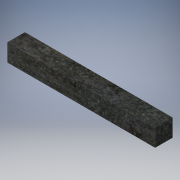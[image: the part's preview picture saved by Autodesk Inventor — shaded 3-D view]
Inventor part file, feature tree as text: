
AUTODESK INVENTOR PART (.ipt)
format: ipt  version: 2019 (Build 230136000, 136)  size: 106,496 bytes
history: native  units: mm
features: extrude x1, sketch x1
ambient origin geometry x8: Origin, YZ Plane, XZ Plane, XY Plane, X Axis, Y Axis, Z Axis, Center Point
bodies: Solid1 (feature_tree)
feature tree (2):
  extrude  "Extrusion1"  Depth=10.0mm
  sketch  "Sketch1"  dims[d0=85.0mm d1=10.0mm d4=75.0mm d5=15.0mm d6=10.0mm d7=0.0mm]
